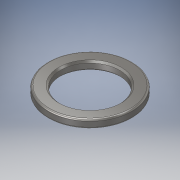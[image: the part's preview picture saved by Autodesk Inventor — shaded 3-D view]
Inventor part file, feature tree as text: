
AUTODESK INVENTOR PART (.ipt)
format: ipt  version: 2019.2 (Build 232265000, 265)  size: 132,608 bytes
history: native  units: mm
features: extrude x1, chamfer x1, fillet x1, sketch x1
ambient origin geometry x8: Origin, YZ Plane, XZ Plane, XY Plane, X Axis, Y Axis, Z Axis, Center Point
bodies: Solid1 (feature_tree)
feature tree (4):
  extrude  "Extrusion1"  Depth=0.1mm
  chamfer  "Chamfer1"  Distance=0.5mm
  fillet  "Fillet1"  Radius=0.1mm
  sketch  "Sketch1"  dims[d0=3.5mm d1=5.0mm d2=0.5mm d3=0.0mm d4=0.1mm d5=2.0mm d6=45.0deg d7=0.1mm]
